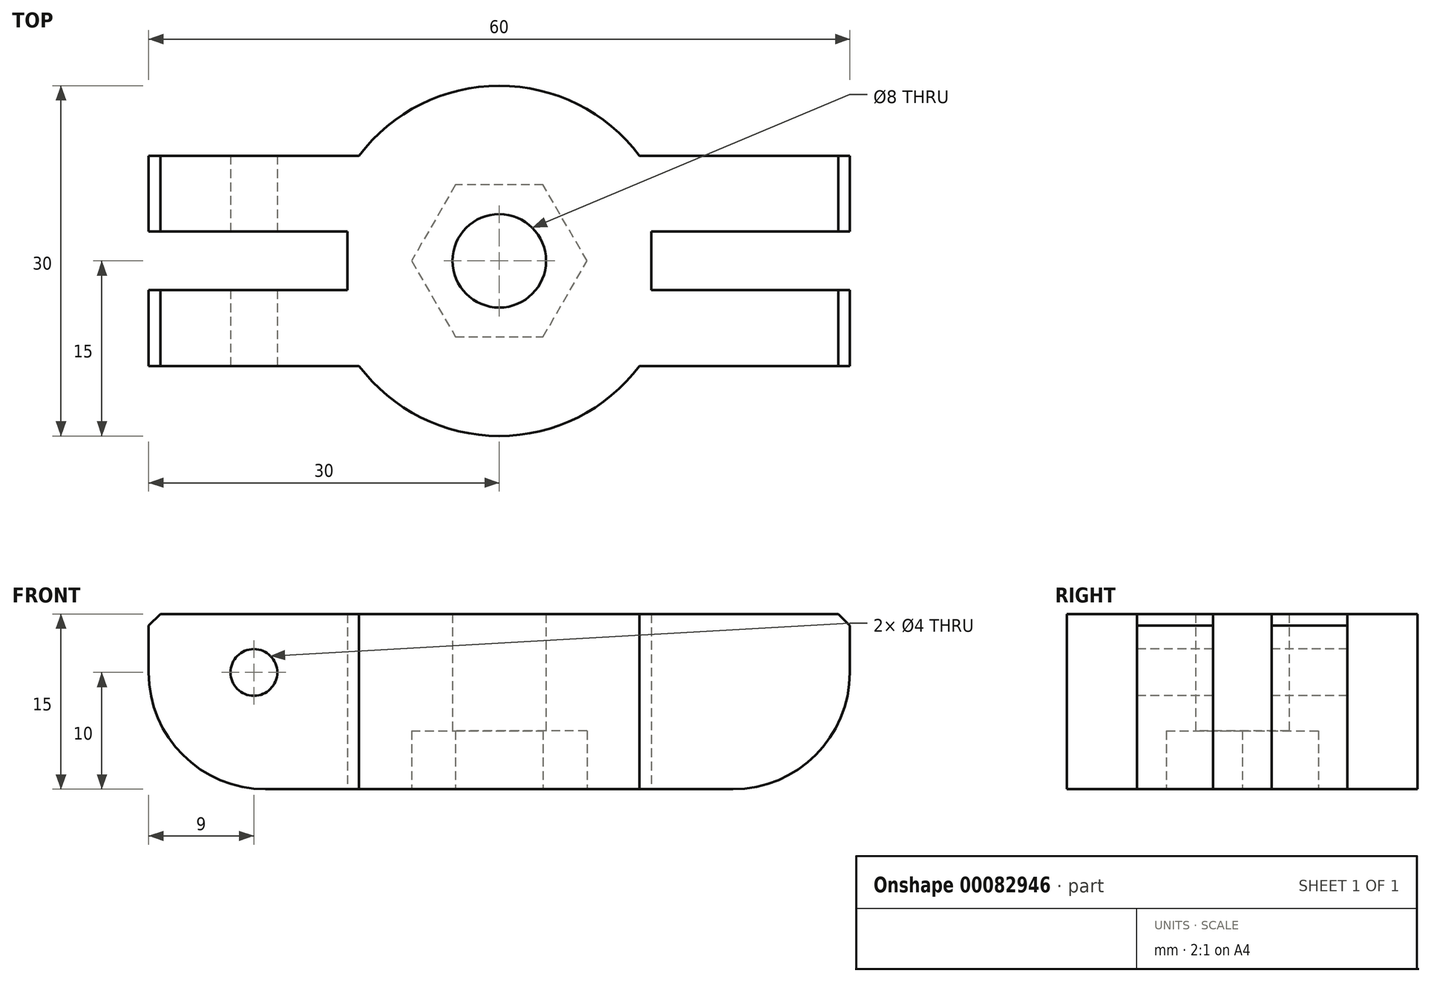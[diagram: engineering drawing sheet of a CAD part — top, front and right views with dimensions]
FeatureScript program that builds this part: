
annotation { "Feature Type Name" : "Feature", "Feature Type Description" : "" }
export const myFeature = defineFeature(function(context is Context, id is Id, definition is map)
    precondition{}
    {
        {
            var Q0;
            Q0=qCreatedBy(makeId("Top.planeOp"),FACE);
            var sketch = newSketch(context, id + "F0", { "sketchPlane" : qUnion([Q0])});
            skArc(sketch, "E0", {"start": v(-12, -9) * mm, "mid": v(0, -15) * mm, "end": v(12, -9) * mm});
            skLineSegment(sketch, "E1.bottom", {"start": v(-30, 9) * mm, "end": v(-12, 9) * mm});
            skLineSegment(sketch, "E2", {"start": v(-30, 9) * mm, "end": v(-30, 2.5) * mm});
            skLineSegment(sketch, "E3", {"start": v(-30, 2.5) * mm, "end": v(-13, 2.5) * mm});
            skLineSegment(sketch, "E4", {"start": v(-13, 2.5) * mm, "end": v(-13, 0) * mm});
            skLineSegment(sketch, "E5.MirrorCS", {"start": v(-13, -2.5) * mm, "end": v(-13, 0) * mm});
            skLineSegment(sketch, "E6.MirrorCS", {"start": v(-30, -2.5) * mm, "end": v(-13, -2.5) * mm});
            skLineSegment(sketch, "E7.MirrorCS", {"start": v(-30, -9) * mm, "end": v(-30, -2.5) * mm});
            skLineSegment(sketch, "E8.MirrorCS", {"start": v(-30, -9) * mm, "end": v(-12, -9) * mm});
            skLineSegment(sketch, "E9.MirrorCS", {"start": v(30, 9) * mm, "end": v(12, 9) * mm});
            skLineSegment(sketch, "E10.MirrorCS", {"start": v(30, 9) * mm, "end": v(30, 2.5) * mm});
            skLineSegment(sketch, "E11.MirrorCS", {"start": v(30, 2.5) * mm, "end": v(13, 2.5) * mm});
            skLineSegment(sketch, "E12.MirrorCS", {"start": v(13, 2.5) * mm, "end": v(13, 0) * mm});
            skLineSegment(sketch, "E13.MirrorCS", {"start": v(13, -2.5) * mm, "end": v(13, 0) * mm});
            skLineSegment(sketch, "E14.MirrorCS", {"start": v(30, -2.5) * mm, "end": v(13, -2.5) * mm});
            skLineSegment(sketch, "E15.MirrorCS", {"start": v(30, -9) * mm, "end": v(30, -2.5) * mm});
            skLineSegment(sketch, "E16.MirrorCS", {"start": v(30, -9) * mm, "end": v(12, -9) * mm});
            skArc(sketch, "E17.trimOffspring", {"start": v(12, 9) * mm, "mid": v(0, 15) * mm, "end": v(-12, 9) * mm});
            skCircle(sketch, "E18", {"center": v(0, 0) * mm, "radius": 4 * mm});
            skSolve(sketch);
        }
        {
            var Q0;
            Q0=makeQuery(id+"F0.imprint","IMPRINT",FACE,{"disambiguationData":[TD([[makeQuery(id+"F0.imprint","IMPRINT",EDGE,{"derivedFrom":sQuery(id+"F0.wireOp",EDGE,"E0")}),1.0]])]});
            extrude(context, id + "F1", {"entities" : qUnion([Q0]), "depth" : 15 * mm});
        }
        {
            var Q0;
            Q0=makeQuery(id+"F1.opExtrude","CAP_FACE",FACE,{"disambiguationData":[OSD([sQuery(id+"F0.wireOp",EDGE,"E0"),sQuery(id+"F0.wireOp",EDGE,"E1.bottom"),sQuery(id+"F0.wireOp",EDGE,"bb04efce-7968-4a81-82cb-dc251339d20a.filletArc"),sQuery(id+"F0.wireOp",EDGE,"E2"),sQuery(id+"F0.wireOp",EDGE,"E3"),sQuery(id+"F0.wireOp",EDGE,"E4"),sQuery(id+"F0.wireOp",EDGE,"E5.MirrorCS"),sQuery(id+"F0.wireOp",EDGE,"E6.MirrorCS"),sQuery(id+"F0.wireOp",EDGE,"E7.MirrorCS"),sQuery(id+"F0.wireOp",EDGE,"a59bf056-13eb-43d5-9a17-3d0f563b8d6f0.MirrorCS"),sQuery(id+"F0.wireOp",EDGE,"E8.MirrorCS"),sQuery(id+"F0.wireOp",EDGE,"E9.MirrorCS"),sQuery(id+"F0.wireOp",EDGE,"519b94bb-44f3-4e2e-8538-fc6604079f360.MirrorCS"),sQuery(id+"F0.wireOp",EDGE,"E10.MirrorCS"),sQuery(id+"F0.wireOp",EDGE,"E11.MirrorCS"),sQuery(id+"F0.wireOp",EDGE,"E12.MirrorCS"),sQuery(id+"F0.wireOp",EDGE,"E13.MirrorCS"),sQuery(id+"F0.wireOp",EDGE,"E14.MirrorCS"),sQuery(id+"F0.wireOp",EDGE,"E15.MirrorCS"),sQuery(id+"F0.wireOp",EDGE,"936b110c-6b04-4bba-ba3b-bad2a98c92be0.MirrorCS"),sQuery(id+"F0.wireOp",EDGE,"E16.MirrorCS"),sQuery(id+"F0.wireOp",EDGE,"E17.trimOffspring"),sQuery(id+"F0.wireOp",EDGE,"E18")])],"isStart":true});
            var sketch = newSketch(context, id + "F2", { "sketchPlane" : qUnion([Q0])});
            skCircle(sketch, "E19.cCircle", {"center": v(0, 0) * mm, "radius": 7.5 * mm, "construction": true});
            skLineSegment(sketch, "E19.0", {"start": v(7.5, 0) * mm, "end": v(3.75, -6.5) * mm});
            skLineSegment(sketch, "E19.1", {"start": v(3.75, -6.5) * mm, "end": v(-3.75, -6.5) * mm});
            skLineSegment(sketch, "E19.2", {"start": v(-3.75, -6.5) * mm, "end": v(-7.5, 0) * mm});
            skLineSegment(sketch, "E19.3", {"start": v(-7.5, 0) * mm, "end": v(-3.75, 6.5) * mm});
            skLineSegment(sketch, "E19.4", {"start": v(-3.75, 6.5) * mm, "end": v(3.75, 6.5) * mm});
            skLineSegment(sketch, "E19.5", {"start": v(3.75, 6.5) * mm, "end": v(7.5, 0) * mm});
            skSolve(sketch);
        }
        {
            var Q0;
            Q0=makeQuery(id+"F2.imprint","IMPRINT",FACE,{"disambiguationData":[TD([[makeQuery(id+"F2.imprint","IMPRINT",EDGE,{"derivedFrom":sQuery(id+"F2.wireOp",EDGE,"E19.0")}),-1.0]])]});
            extrude(context, id + "F3", {"entities" : qUnion([Q0]), "operationType" : NewBodyOperationType.REMOVE, "oppositeDirection" : true, "depth" : 5 * mm});
        }
        {
            var Q0;
            Q0=makeQuery(id+"F1.opExtrude","SWEPT_FACE",FACE,{"disambiguationData":[OSD([sQuery(id+"F0.wireOp",EDGE,"E8.MirrorCS")])]});
            var sketch = newSketch(context, id + "F4", { "sketchPlane" : qUnion([Q0])});
            skCircle(sketch, "E20", {"center": v(-21, 10) * mm, "radius": 2 * mm});
            skCircle(sketch, "E21.MirrorC", {"center": v(21, 10) * mm, "radius": 2 * mm});
            skSolve(sketch);
        }
        {
            var Q0;
            Q0=makeQuery(id+"F4.imprint","IMPRINT",FACE,{"disambiguationData":[TD([[makeQuery(id+"F4.imprint","IMPRINT",EDGE,{"derivedFrom":sQuery(id+"F4.wireOp",EDGE,"E20")}),1.0]])]});
            var Q1;
            Q1=makeQuery(id+"F4.imprint","IMPRINT",FACE,{"disambiguationData":[TD([[makeQuery(id+"F4.imprint","IMPRINT",EDGE,{"derivedFrom":sQuery(id+"F4.wireOp",EDGE,"E21.MirrorC")}),-1.0]])]});
            var Q2;
            Q2=sQuery(id+"F4.wireOp",EDGE,"E20");
            var Q3;
            Q3=sQuery(id+"F4.wireOp",EDGE,"E21.MirrorC");
            extrude(context, id + "F5", {"entities" : qUnion([Q0, Q1]), "operationType" : NewBodyOperationType.REMOVE, "surfaceEntities" : qUnion([Q2, Q3]), "endBound" : BoundingType.THROUGH_ALL, "oppositeDirection" : true, "depth" : 25 * mm});
        }
        {
            var Q0;
            Q0=makeQuery(id+"F1.opExtrude","CAP_EDGE",EDGE,{"disambiguationData":[OSD([sQuery(id+"F0.wireOp",EDGE,"E7.MirrorCS")])],"isStart":true});
            var Q1;
            Q1=makeQuery(id+"F1.opExtrude","CAP_EDGE",EDGE,{"disambiguationData":[OSD([sQuery(id+"F0.wireOp",EDGE,"E2")])],"isStart":true});
            var Q2;
            Q2=makeQuery(id+"F1.opExtrude","CAP_EDGE",EDGE,{"disambiguationData":[OSD([sQuery(id+"F0.wireOp",EDGE,"E15.MirrorCS")])],"isStart":true});
            var Q3;
            Q3=makeQuery(id+"F1.opExtrude","CAP_EDGE",EDGE,{"disambiguationData":[OSD([sQuery(id+"F0.wireOp",EDGE,"E10.MirrorCS")])],"isStart":true});
            fillet(context, id + "F6", {"entities" : qUnion([Q0, Q1, Q2, Q3]), "radius" : 10 * mm, "tangentPropagation" : true, "allowEdgeOverflow" : false});
        }
        {
            var Q0;
            Q0=makeQuery(id+"F1.opExtrude","CAP_EDGE",EDGE,{"disambiguationData":[OSD([sQuery(id+"F0.wireOp",EDGE,"E2")])],"isStart":false});
            var Q1;
            Q1=makeQuery(id+"F1.opExtrude","CAP_EDGE",EDGE,{"disambiguationData":[OSD([sQuery(id+"F0.wireOp",EDGE,"E7.MirrorCS")])],"isStart":false});
            var Q2;
            Q2=makeQuery(id+"F1.opExtrude","CAP_EDGE",EDGE,{"disambiguationData":[OSD([sQuery(id+"F0.wireOp",EDGE,"E10.MirrorCS")])],"isStart":false});
            var Q3;
            Q3=makeQuery(id+"F1.opExtrude","CAP_EDGE",EDGE,{"disambiguationData":[OSD([sQuery(id+"F0.wireOp",EDGE,"E15.MirrorCS")])],"isStart":false});
            chamfer(context, id + "F7", {"entities" : qUnion([Q0, Q1, Q2, Q3]), "width" : 1 * mm, "tangentPropagation" : true});
        }
    });
